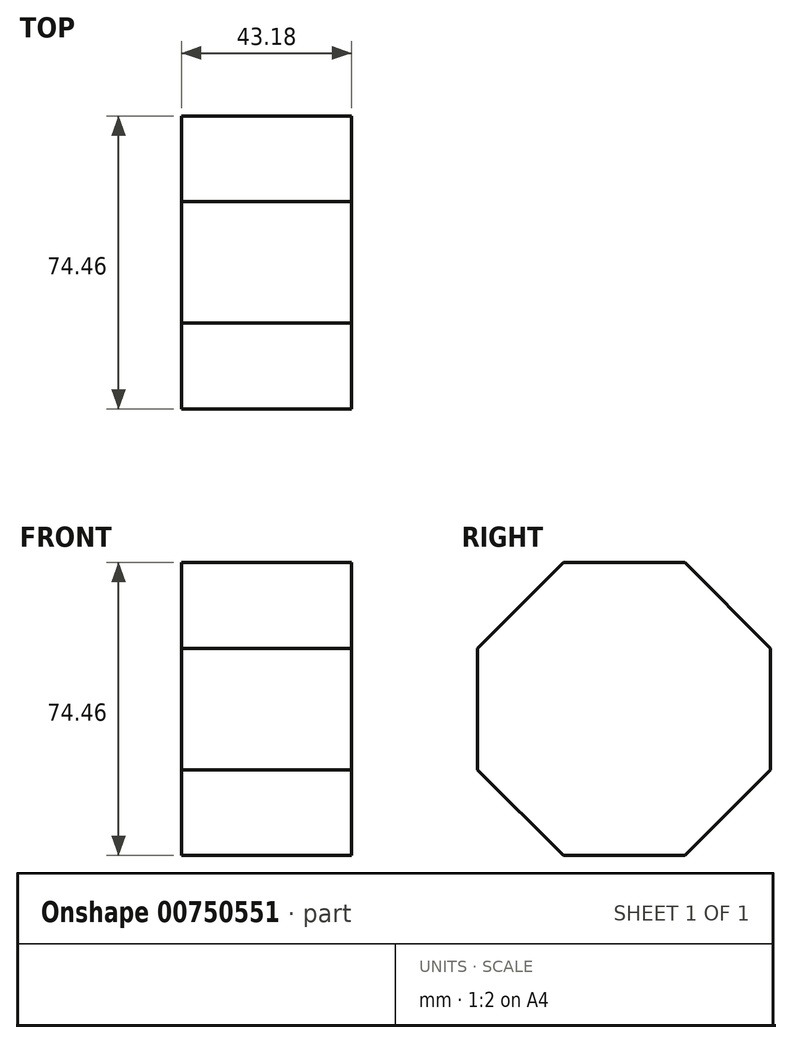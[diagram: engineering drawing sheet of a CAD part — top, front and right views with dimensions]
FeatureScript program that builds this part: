
annotation { "Feature Type Name" : "Feature", "Feature Type Description" : "" }
export const myFeature = defineFeature(function(context is Context, id is Id, definition is map)
    precondition{}
    {
        {
            var Q0;
            Q0=qCreatedBy(makeId("Right.planeOp"),FACE);
            var sketch = newSketch(context, id + "F0", { "sketchPlane" : qUnion([Q0])});
            skLineSegment(sketch, "E0.0", {"start": v(-37.23, -15.42) * mm, "end": v(-37.23, 15.42) * mm});
            skLineSegment(sketch, "E0.1", {"start": v(-37.23, 15.42) * mm, "end": v(-15.42, 37.23) * mm});
            skLineSegment(sketch, "E0.2", {"start": v(-15.42, 37.23) * mm, "end": v(15.42, 37.23) * mm});
            skLineSegment(sketch, "E0.3", {"start": v(15.42, 37.23) * mm, "end": v(37.23, 15.42) * mm});
            skLineSegment(sketch, "E0.4", {"start": v(37.23, 15.42) * mm, "end": v(37.23, -15.42) * mm});
            skLineSegment(sketch, "E0.5", {"start": v(37.23, -15.42) * mm, "end": v(15.42, -37.23) * mm});
            skLineSegment(sketch, "E0.6", {"start": v(15.42, -37.23) * mm, "end": v(-15.42, -37.23) * mm});
            skLineSegment(sketch, "E0.7", {"start": v(-15.42, -37.23) * mm, "end": v(-37.23, -15.42) * mm});
            skPoint(sketch, "E0.0.midPoint", {"position": v(-37.23, 0) * mm});
            skSolve(sketch);
        }
        {
            var Q0;
            Q0=makeQuery(id+"F0.imprint","IMPRINT",FACE,{"disambiguationData":[TD([[makeQuery(id+"F0.imprint","IMPRINT",EDGE,{"derivedFrom":sQuery(id+"F0.wireOp",EDGE,"E0.0")}),-1.0]])]});
            extrude(context, id + "F1", {"entities" : qUnion([Q0]), "depth" : 43.18 * mm, "offsetDistance" : 25.4 * mm});
        }
    });
